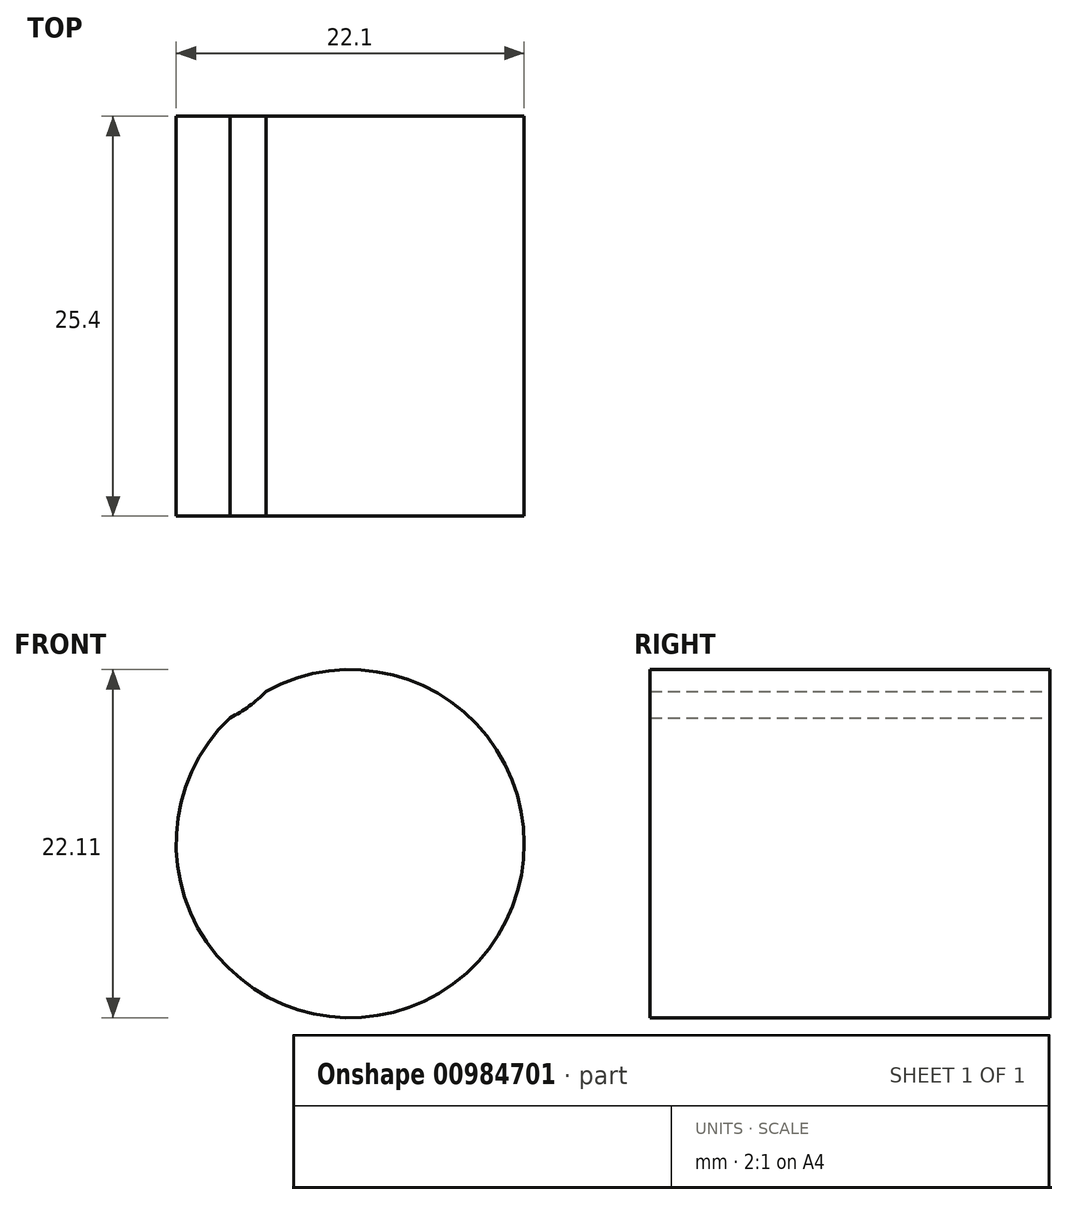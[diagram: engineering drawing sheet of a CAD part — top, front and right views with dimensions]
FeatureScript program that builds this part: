
annotation { "Feature Type Name" : "Feature", "Feature Type Description" : "" }
export const myFeature = defineFeature(function(context is Context, id is Id, definition is map)
    precondition{}
    {
        {
            var Q0;
            Q0=qCreatedBy(makeId("Front.planeOp"),FACE);
            var sketch = newSketch(context, id + "F0", { "sketchPlane" : qUnion([Q0])});
            skCircle(sketch, "E0", {"center": v(0, 4.44) * mm, "radius": 11.05 * mm});
            skCircle(sketch, "E1", {"center": v(-11, 19.42) * mm, "radius": 7.75 * mm});
            skSolve(sketch);
        }
        {
            var Q0;
            {var subQ0=sQuery(id+"F0.wireOp",EDGE,"E1");var subQ1=sQuery(id+"F0.wireOp",EDGE,"E0");var subQ2=makeQuery(id+"F0.imprint","INTERSECT",VERTEX,{"disambiguationData":[OD(0.0)],"derivedFrom":[subQ1,subQ0]});Q0=makeQuery(id+"F0.imprint","IMPRINT",FACE,{"disambiguationData":[TD([[makeQuery(id+"F0.imprint","IMPRINT",EDGE,{"disambiguationData":[TD([[subQ2,-1.0]])],"derivedFrom":subQ1}),1.0]])]});}
            extrude(context, id + "F1", {"entities" : qUnion([Q0]), "depth" : 25.4 * mm, "offsetDistance" : 25.4 * mm});
        }
    });
